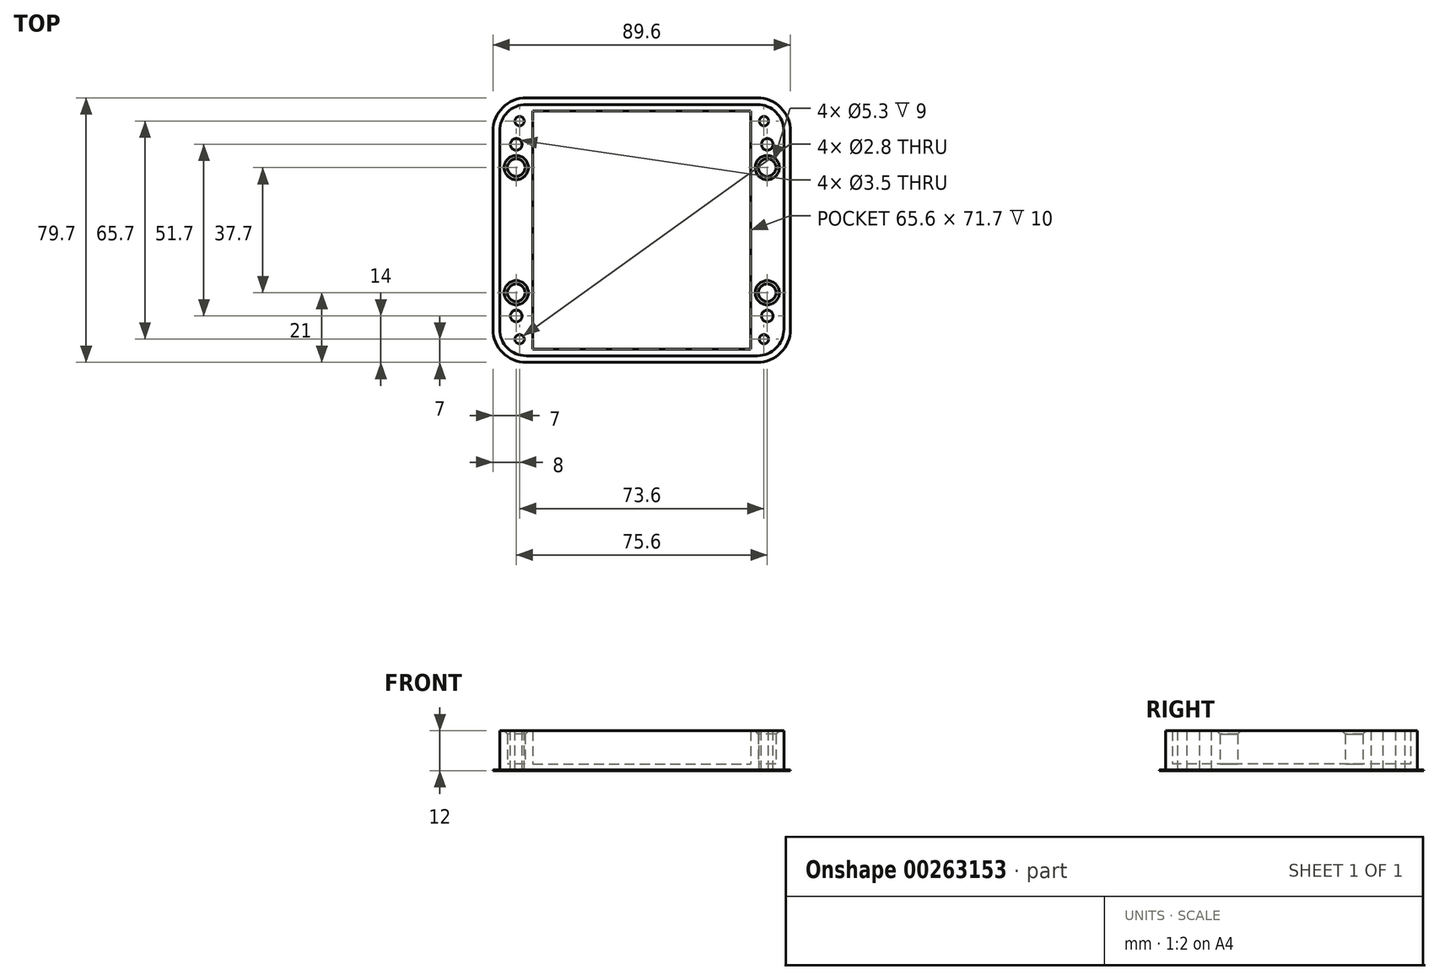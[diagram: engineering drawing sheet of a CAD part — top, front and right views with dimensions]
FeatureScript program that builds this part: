
annotation { "Feature Type Name" : "Feature", "Feature Type Description" : "" }
export const myFeature = defineFeature(function(context is Context, id is Id, definition is map)
    precondition{}
    {
        {
            var Q0;
            Q0=qCreatedBy(makeId("Top.planeOp"),FACE);
            var sketch = newSketch(context, id + "F0", { "sketchPlane" : qUnion([Q0])});
            skLineSegment(sketch, "E0.bottom", {"start": v(-34.8, 37.85) * mm, "end": v(34.8, 37.85) * mm});
            skLineSegment(sketch, "E0.top", {"start": v(-34.8, -37.85) * mm, "end": v(34.8, -37.85) * mm});
            skLineSegment(sketch, "E1.bottom", {"start": v(-32.3, 35.35) * mm, "end": v(32.3, 35.35) * mm, "construction": true});
            skLineSegment(sketch, "E1.top", {"start": v(-32.3, -35.35) * mm, "end": v(32.3, -35.35) * mm, "construction": true});
            skLineSegment(sketch, "E1.left", {"start": v(-32.3, 35.35) * mm, "end": v(-32.3, -35.35) * mm, "construction": true});
            skLineSegment(sketch, "E1.right", {"start": v(32.3, 35.35) * mm, "end": v(32.3, -35.35) * mm, "construction": true});
            skLineSegment(sketch, "E2", {"start": v(-42.8, 29.85) * mm, "end": v(-42.8, -29.85) * mm});
            skLineSegment(sketch, "E3", {"start": v(42.8, 29.85) * mm, "end": v(42.8, -29.85) * mm});
            skArc(sketch, "E4", {"start": v(-34.8, 37.85) * mm, "mid": v(-40.46, 35.5) * mm, "end": v(-42.8, 29.85) * mm});
            skArc(sketch, "E5", {"start": v(42.8, 29.85) * mm, "mid": v(40.46, 35.5) * mm, "end": v(34.8, 37.85) * mm});
            skArc(sketch, "E6", {"start": v(34.8, -37.85) * mm, "mid": v(40.46, -35.5) * mm, "end": v(42.8, -29.85) * mm});
            skArc(sketch, "E7", {"start": v(-42.8, -29.85) * mm, "mid": v(-40.46, -35.5) * mm, "end": v(-34.8, -37.85) * mm});
            skSolve(sketch);
        }
        {
            var Q0;
            Q0=qSketchRegion(id+"F0",true);
            extrude(context, id + "F1", {"entities" : qUnion([Q0]), "depth" : 2 * mm});
        }
        {
            var Q0;
            Q0=makeQuery(id+"F1.opExtrude","CAP_FACE",FACE,{"disambiguationData":[OSD([sQuery(id+"F0.wireOp",EDGE,"E0.bottom"),sQuery(id+"F0.wireOp",EDGE,"E0.top"),sQuery(id+"F0.wireOp",EDGE,"E2"),sQuery(id+"F0.wireOp",EDGE,"E3"),sQuery(id+"F0.wireOp",EDGE,"E4"),sQuery(id+"F0.wireOp",EDGE,"E5"),sQuery(id+"F0.wireOp",EDGE,"E6"),sQuery(id+"F0.wireOp",EDGE,"E7")])],"isStart":false});
            var sketch = newSketch(context, id + "F2", { "sketchPlane" : qUnion([Q0])});
            skLineSegment(sketch, "E8", {"start": v(-42.8, 29.85) * mm, "end": v(-42.8, -29.85) * mm});
            skLineSegment(sketch, "E9", {"start": v(-34.8, 37.85) * mm, "end": v(34.8, 37.85) * mm});
            skLineSegment(sketch, "E10", {"start": v(42.8, 29.85) * mm, "end": v(42.8, -29.85) * mm});
            skLineSegment(sketch, "E11", {"start": v(-34.8, -37.85) * mm, "end": v(34.8, -37.85) * mm});
            skArc(sketch, "E12", {"start": v(-42.8, -29.85) * mm, "mid": v(-40.46, -35.5) * mm, "end": v(-34.8, -37.85) * mm});
            skArc(sketch, "E13", {"start": v(-34.8, 37.85) * mm, "mid": v(-40.46, 35.5) * mm, "end": v(-42.8, 29.85) * mm});
            skArc(sketch, "E14", {"start": v(42.8, 29.85) * mm, "mid": v(40.46, 35.5) * mm, "end": v(34.8, 37.85) * mm});
            skArc(sketch, "E15", {"start": v(34.8, -37.85) * mm, "mid": v(40.46, -35.5) * mm, "end": v(42.8, -29.85) * mm});
            skLineSegment(sketch, "E16.bottom", {"start": v(-32.8, 35.85) * mm, "end": v(32.8, 35.85) * mm});
            skLineSegment(sketch, "E16.top", {"start": v(-32.8, -35.85) * mm, "end": v(32.8, -35.85) * mm});
            skLineSegment(sketch, "E16.left", {"start": v(-32.8, 35.85) * mm, "end": v(-32.8, -35.85) * mm});
            skLineSegment(sketch, "E16.right", {"start": v(32.8, 35.85) * mm, "end": v(32.8, -35.85) * mm});
            skLineSegment(sketch, "E17", {"start": v(-42.8, -29.85) * mm, "end": v(-34.8, -29.85) * mm, "construction": true});
            skCircle(sketch, "E18", {"center": v(-37.8, -18.85) * mm, "radius": 2.65 * mm});
            skCircle(sketch, "E19.MirrorC", {"center": v(37.8, -18.85) * mm, "radius": 2.65 * mm});
            skCircle(sketch, "E20.MirrorC", {"center": v(-37.8, 18.85) * mm, "radius": 2.65 * mm});
            skCircle(sketch, "E21.MirrorC", {"center": v(37.8, 18.85) * mm, "radius": 2.65 * mm});
            skSolve(sketch);
        }
        {
            var Q0;
            Q0=qSketchRegion(id+"F2",true);
            extrude(context, id + "F3", {"entities" : qUnion([Q0]), "operationType" : NewBodyOperationType.ADD, "depth" : 10 * mm});
        }
        {
            var Q0;
            Q0=makeQuery(id+"F3.opExtrude","CAP_FACE",FACE,{"disambiguationData":[OSD([sQuery(id+"F2.wireOp",EDGE,"E8"),sQuery(id+"F2.wireOp",EDGE,"E9"),sQuery(id+"F2.wireOp",EDGE,"E10"),sQuery(id+"F2.wireOp",EDGE,"E11"),sQuery(id+"F2.wireOp",EDGE,"E12"),sQuery(id+"F2.wireOp",EDGE,"E13"),sQuery(id+"F2.wireOp",EDGE,"E14"),sQuery(id+"F2.wireOp",EDGE,"E15"),sQuery(id+"F2.wireOp",EDGE,"E16.bottom"),sQuery(id+"F2.wireOp",EDGE,"E16.top"),sQuery(id+"F2.wireOp",EDGE,"E16.left"),sQuery(id+"F2.wireOp",EDGE,"E16.right")])],"isStart":false});
            var sketch = newSketch(context, id + "F4", { "sketchPlane" : qUnion([Q0])});
            skCircle(sketch, "E22", {"center": v(-36.8, -32.85) * mm, "radius": 1.4 * mm});
            skCircle(sketch, "E23.MirrorC", {"center": v(36.8, -32.85) * mm, "radius": 1.4 * mm});
            skCircle(sketch, "E24.MirrorC", {"center": v(-36.8, 32.85) * mm, "radius": 1.4 * mm});
            skCircle(sketch, "E25.MirrorC", {"center": v(36.8, 32.85) * mm, "radius": 1.4 * mm});
            skCircle(sketch, "E26", {"center": v(-37.8, -25.85) * mm, "radius": 1.75 * mm});
            skCircle(sketch, "E27.MirrorC", {"center": v(37.8, -25.85) * mm, "radius": 1.75 * mm});
            skCircle(sketch, "E28.MirrorC", {"center": v(-37.8, 25.85) * mm, "radius": 1.75 * mm});
            skCircle(sketch, "E29.MirrorC", {"center": v(37.8, 25.85) * mm, "radius": 1.75 * mm});
            skSolve(sketch);
        }
        {
            var Q0;
            Q0=qSketchRegion(id+"F4",true);
            var Q1;
            Q1=makeQuery(id+"F1.opExtrude","CAP_FACE",FACE,{"disambiguationData":[OSD([sQuery(id+"F0.wireOp",EDGE,"E0.bottom"),sQuery(id+"F0.wireOp",EDGE,"E0.top"),sQuery(id+"F0.wireOp",EDGE,"E2"),sQuery(id+"F0.wireOp",EDGE,"E3"),sQuery(id+"F0.wireOp",EDGE,"E4"),sQuery(id+"F0.wireOp",EDGE,"E5"),sQuery(id+"F0.wireOp",EDGE,"E6"),sQuery(id+"F0.wireOp",EDGE,"E7")])],"isStart":true});
            extrude(context, id + "F5", {"entities" : qUnion([Q0]), "operationType" : NewBodyOperationType.REMOVE, "endBound" : BoundingType.UP_TO_SURFACE, "oppositeDirection" : true, "endBoundEntityFace" : qUnion([Q1]), "depth" : 25 * mm});
        }
        {
            var Q0;
            Q0=makeQuery(id+"F3.opExtrude","CAP_EDGE",EDGE,{"disambiguationData":[OSD([sQuery(id+"F2.wireOp",EDGE,"E20.MirrorC")])],"isStart":false});
            var Q1;
            Q1=makeQuery(id+"F3.opExtrude","CAP_EDGE",EDGE,{"disambiguationData":[OSD([sQuery(id+"F2.wireOp",EDGE,"E21.MirrorC")])],"isStart":false});
            var Q2;
            Q2=makeQuery(id+"F3.opExtrude","CAP_EDGE",EDGE,{"disambiguationData":[OSD([sQuery(id+"F2.wireOp",EDGE,"E19.MirrorC")])],"isStart":false});
            var Q3;
            Q3=makeQuery(id+"F3.opExtrude","CAP_EDGE",EDGE,{"disambiguationData":[OSD([sQuery(id+"F2.wireOp",EDGE,"E18")])],"isStart":false});
            chamfer(context, id + "F6", {"entities" : qUnion([Q0, Q1, Q2, Q3]), "width" : 1 * mm, "tangentPropagation" : true});
        }
        {
            var Q0;
            Q0=makeQuery(id+"F1.opExtrude","CAP_FACE",FACE,{"disambiguationData":[OSD([sQuery(id+"F0.wireOp",EDGE,"E0.bottom"),sQuery(id+"F0.wireOp",EDGE,"E0.top"),sQuery(id+"F0.wireOp",EDGE,"E2"),sQuery(id+"F0.wireOp",EDGE,"E3"),sQuery(id+"F0.wireOp",EDGE,"E4"),sQuery(id+"F0.wireOp",EDGE,"E5"),sQuery(id+"F0.wireOp",EDGE,"E6"),sQuery(id+"F0.wireOp",EDGE,"E7")])],"isStart":true});
            var sketch = newSketch(context, id + "F7", { "sketchPlane" : qUnion([Q0])});
            skLineSegment(sketch, "E30.bottom", {"start": v(-34.8, 39.85) * mm, "end": v(34.8, 39.85) * mm});
            skLineSegment(sketch, "E30.top", {"start": v(-34.8, -39.85) * mm, "end": v(34.8, -39.85) * mm});
            skLineSegment(sketch, "E30.left", {"start": v(-44.8, 29.85) * mm, "end": v(-44.8, -29.85) * mm});
            skLineSegment(sketch, "E30.right", {"start": v(44.8, 29.85) * mm, "end": v(44.8, -29.85) * mm});
            skArc(sketch, "E31", {"start": v(-34.8, 39.85) * mm, "mid": v(-41.87, 36.92) * mm, "end": v(-44.8, 29.85) * mm});
            skArc(sketch, "E32", {"start": v(44.8, 29.85) * mm, "mid": v(41.87, 36.92) * mm, "end": v(34.8, 39.85) * mm});
            skArc(sketch, "E33", {"start": v(34.8, -39.85) * mm, "mid": v(41.87, -36.92) * mm, "end": v(44.8, -29.85) * mm});
            skArc(sketch, "E34", {"start": v(-44.8, -29.85) * mm, "mid": v(-41.87, -36.92) * mm, "end": v(-34.8, -39.85) * mm});
            skLineSegment(sketch, "E35", {"start": v(-42.8, 29.85) * mm, "end": v(-42.8, -29.85) * mm});
            skLineSegment(sketch, "E36", {"start": v(34.8, 37.85) * mm, "end": v(-34.8, 37.85) * mm});
            skLineSegment(sketch, "E37", {"start": v(42.8, 29.85) * mm, "end": v(42.8, -29.85) * mm});
            skLineSegment(sketch, "E38", {"start": v(-34.8, -37.85) * mm, "end": v(34.8, -37.85) * mm});
            skArc(sketch, "E39", {"start": v(-42.8, -29.85) * mm, "mid": v(-40.46, -35.5) * mm, "end": v(-34.8, -37.85) * mm});
            skArc(sketch, "E40", {"start": v(34.8, -37.85) * mm, "mid": v(40.46, -35.5) * mm, "end": v(42.8, -29.85) * mm});
            skArc(sketch, "E41", {"start": v(42.8, 29.85) * mm, "mid": v(40.46, 35.5) * mm, "end": v(34.8, 37.85) * mm});
            skArc(sketch, "E42", {"start": v(-34.8, 37.85) * mm, "mid": v(-40.46, 35.5) * mm, "end": v(-42.8, 29.85) * mm});
            skSolve(sketch);
        }
        {
            var Q0;
            Q0 = qSketchRegion(id + "F7", true);
            extrude(context, id + "F8", {"entities" : qUnion([Q0]), "operationType" : NewBodyOperationType.ADD, "oppositeDirection" : true, "depth" : 0.2 * mm});
        }
    });
